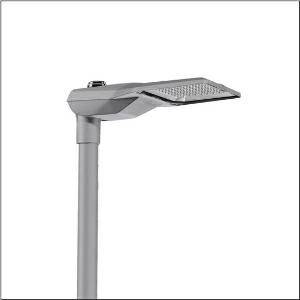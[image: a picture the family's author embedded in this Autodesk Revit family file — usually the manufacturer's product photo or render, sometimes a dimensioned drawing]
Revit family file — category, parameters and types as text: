
# Revit family: streetlight_sl_21_midi___st0_8a_5xe7c37n08nb_761f
name_source: partatom
category: Lighting Fixtures
units: mm (PartAtom-declared; Revit-internal decimal feet)

## family parameters
Cut with Voids When Loaded = No
Host = Face
Light Source = No
Part Type = Normal
Room Calculation Point = No
Round Connector Dimension = Use Diameter
Shared = No

## types (1)
- --- (1 x LED, 22700 lm, 151.2 W, 3000K)
    Apparent Load = 151 VA
    CIE Flux Codes = 41 75 97 100 100
    Color Rendering = 70
    Color Temperature = 3000K
    Default Elevation = 1800 mm
    Description = Streetlight SL 21 midi, mast luminaire, primary light control with lens, of PMMA, primary optical cover: cover, of toughened safety glass, transparent, light distribution: ST0.8a, light emission: direct distribution, primary light characteristic: asymmetric, installation type: side-entry, LED, 3G 2.5mm², High Power LED, rated luminous flux: 22.700lm, luminous efficacy: 150lm/W, light colour: 730, colour temperature: 3000K, control: overheat protection, presetting dimming linear, constant luminous flux control, time-dependent luminous flux control, flexible luminous flux parameterisation, mains connection: 220..240V, AC, 50/60Hz, connection cable pre-assembled, cable length: 12,5m, wiring characteristics: H05VV-F, start of lifetime: 151W, end of service life: 157W, reduction: 70W, luminaire housing, of diecast aluminium (EN AC-44300), powder-coated, Siteco® metallic grey (DB 702S), corrosivity category C5 mid according to DIN EN ISO 12944, multi-level sealing system, sealing non-destructively replaceable, inclination adjustable: 0°, 5°, 10°, 15°, length: 644mm, width: 335mm, height: 110mm, spigot size: 42mm (side-entry), protection rating (complete): IP66, insulation class (complete): insulation class I (protective earthing), certification: CE, ENEC, ENEC+, VDE, impact resistance: IK09, permissible operating ambient temperature for outdoor applications: -40..+50°C, standard-compliant lighting for roads and squares, packaging unit: 1 piece

Light Distribution: ST0.8a
    Height = 111 mm
    Lamp = 1 x LED
    Lamp Light Flux = 22700 lm
    Lamp Power = 151.2 W
    Lamp count = 1
    Length = 644 mm
    Luminous efficacy = 150 lm/W
    Manufacturer = Siteco
    ModVariant = No
    Model = 5XE7C37N08NB
    Number of Poles = 1
    OnlyDefault = Yes
    Power Factor = 1
    Product Name = Streetlight SL 21 midi | ST0.8a
    Product group = mast luminaire | pylon top
    ProductGroupID = 6100
    Protection Class = Protection class I
    Protection Degree = IP 66
    RLX_Detail_Level = 1
    RLX_Emergency_Light_Flux = 0 lm
    RLX_Emergency_Type = 0
    RLX_Emergency_Type_DB = No
    RlxData = <blob elided: 90717 chars, md5=82cc7e87>
    Socket = socket
    Standby Power = 0 W
    System Light Flux = 22700 lm
    System Power = 151 W
    Type Comments = factory setting: luminous flux: 100 % | dim-lin: 254 | 802 mA
    Type Image = l_1294377.jpg
    URL = http://relux.com
    VarID = @adj_083251
    Voltage = 0 V
    Weight = 0.00 kg
    Width = 336 mm

## geometry (parser evidence)
native form markers: Blend x4, Sweep x11
no freeform markers — native parametric forms only
